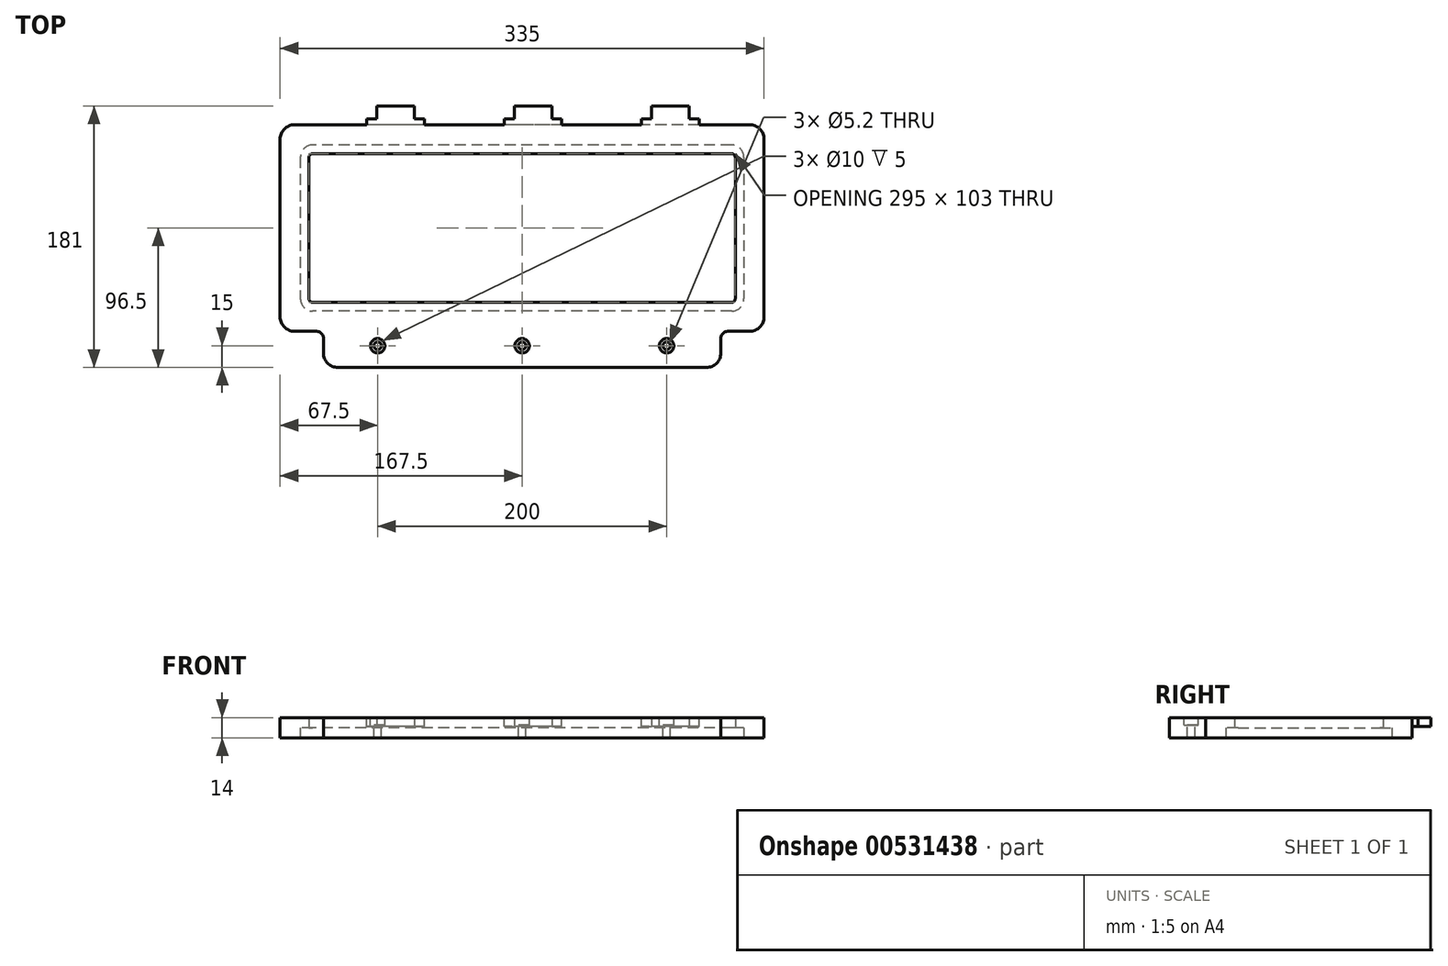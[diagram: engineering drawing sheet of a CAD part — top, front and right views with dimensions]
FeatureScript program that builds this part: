
annotation { "Feature Type Name" : "Feature", "Feature Type Description" : "" }
export const myFeature = defineFeature(function(context is Context, id is Id, definition is map)
    precondition{}
    {
        {
            var Q0;
            Q0=qCreatedBy(makeId("Top.planeOp"),FACE);
            var sketch = newSketch(context, id + "F0", { "sketchPlane" : qUnion([Q0])});
            skLineSegment(sketch, "E0.bottom", {"start": v(145, -51.5) * mm, "end": v(-145, -51.5) * mm});
            skLineSegment(sketch, "E0.top", {"start": v(145, 51.5) * mm, "end": v(-145, 51.5) * mm});
            skLineSegment(sketch, "E0.left", {"start": v(147.5, -49) * mm, "end": v(147.5, 49) * mm});
            skLineSegment(sketch, "E0.right", {"start": v(-147.5, -49) * mm, "end": v(-147.5, 49) * mm});
            skPoint(sketch, "E0.middle", {"position": v(0, 0) * mm});
            skPoint(sketch, "E1.visualSharp", {"position": v(-147.5, 51.5) * mm});
            skArc(sketch, "E1.filletArc", {"start": v(-145, 51.5) * mm, "mid": v(-146.77, 50.77) * mm, "end": v(-147.5, 49) * mm});
            skPoint(sketch, "E2.visualSharp", {"position": v(-147.5, -51.5) * mm});
            skArc(sketch, "E2.filletArc", {"start": v(-147.5, -49) * mm, "mid": v(-146.77, -50.77) * mm, "end": v(-145, -51.5) * mm});
            skPoint(sketch, "E3.visualSharp", {"position": v(147.5, -51.5) * mm});
            skArc(sketch, "E3.filletArc", {"start": v(145, -51.5) * mm, "mid": v(146.77, -50.77) * mm, "end": v(147.5, -49) * mm});
            skPoint(sketch, "E4.visualSharp", {"position": v(147.5, 51.5) * mm});
            skArc(sketch, "E4.filletArc", {"start": v(147.5, 49) * mm, "mid": v(146.77, 50.77) * mm, "end": v(145, 51.5) * mm});
            skLineSegment(sketch, "E5.bottom", {"start": v(167.5, -71.5) * mm, "end": v(137.5, -71.5) * mm});
            skLineSegment(sketch, "E5.top", {"start": v(167.5, 71.5) * mm, "end": v(-167.5, 71.5) * mm});
            skLineSegment(sketch, "E5.left", {"start": v(167.5, -71.5) * mm, "end": v(167.5, 71.5) * mm});
            skLineSegment(sketch, "E5.right", {"start": v(-167.5, -71.5) * mm, "end": v(-167.5, 71.5) * mm});
            skLineSegment(sketch, "E6.top", {"start": v(-137.5, -96.5) * mm, "end": v(137.5, -96.5) * mm});
            skLineSegment(sketch, "E6.left", {"start": v(-137.5, -71.5) * mm, "end": v(-137.5, -96.5) * mm});
            skLineSegment(sketch, "E6.right", {"start": v(137.5, -71.5) * mm, "end": v(137.5, -96.5) * mm});
            skLineSegment(sketch, "E7.trimOffspring", {"start": v(-137.5, -71.5) * mm, "end": v(-167.5, -71.5) * mm});
            skSolve(sketch);
        }
        {
            var Q0;
            Q0=makeQuery(id+"F0.imprint","IMPRINT",FACE,{"disambiguationData":[TD([[makeQuery(id+"F0.imprint","IMPRINT",EDGE,{"derivedFrom":sQuery(id+"F0.wireOp",EDGE,"E0.bottom")}),1.0]])]});
            extrude(context, id + "F1", {"entities" : qUnion([Q0]), "depth" : 14 * mm, "offsetDistance" : 25 * mm});
        }
        {
            var Q0;
            Q0=makeQuery(id+"F1.opExtrude","CAP_FACE",FACE,{"disambiguationData":[OSD([sQuery(id+"F0.wireOp",EDGE,"E0.bottom"),sQuery(id+"F0.wireOp",EDGE,"E0.top"),sQuery(id+"F0.wireOp",EDGE,"E0.left"),sQuery(id+"F0.wireOp",EDGE,"E0.right"),sQuery(id+"F0.wireOp",EDGE,"E1.filletArc"),sQuery(id+"F0.wireOp",EDGE,"E2.filletArc"),sQuery(id+"F0.wireOp",EDGE,"E3.filletArc"),sQuery(id+"F0.wireOp",EDGE,"E4.filletArc"),sQuery(id+"F0.wireOp",EDGE,"E5.bottom"),sQuery(id+"F0.wireOp",EDGE,"E5.top"),sQuery(id+"F0.wireOp",EDGE,"E5.left"),sQuery(id+"F0.wireOp",EDGE,"E5.right")])],"isStart":true});
            var sketch = newSketch(context, id + "F2", { "sketchPlane" : qUnion([Q0])});
            skLineSegment(sketch, "E8.bottom", {"start": v(145, -57.5) * mm, "end": v(-145, -57.5) * mm});
            skLineSegment(sketch, "E8.top", {"start": v(145, 57.5) * mm, "end": v(-145, 57.5) * mm});
            skLineSegment(sketch, "E8.left", {"start": v(153.5, -49) * mm, "end": v(153.5, 49) * mm});
            skLineSegment(sketch, "E8.right", {"start": v(-153.5, -49) * mm, "end": v(-153.5, 49) * mm});
            skPoint(sketch, "E8.middle", {"position": v(0, 0) * mm});
            skPoint(sketch, "E9.visualSharp", {"position": v(-153.5, 57.5) * mm});
            skArc(sketch, "E9.filletArc", {"start": v(-145, 57.5) * mm, "mid": v(-151.01, 55.01) * mm, "end": v(-153.5, 49) * mm});
            skPoint(sketch, "E10.visualSharp", {"position": v(153.5, 57.5) * mm});
            skArc(sketch, "E10.filletArc", {"start": v(153.5, 49) * mm, "mid": v(151.01, 55.01) * mm, "end": v(145, 57.5) * mm});
            skPoint(sketch, "E11.visualSharp", {"position": v(153.5, -57.5) * mm});
            skArc(sketch, "E11.filletArc", {"start": v(145, -57.5) * mm, "mid": v(151.01, -55.01) * mm, "end": v(153.5, -49) * mm});
            skPoint(sketch, "E12.visualSharp", {"position": v(-153.5, -57.5) * mm});
            skArc(sketch, "E12.filletArc", {"start": v(-153.5, -49) * mm, "mid": v(-151.01, -55.01) * mm, "end": v(-145, -57.5) * mm});
            skSolve(sketch);
        }
        {
            var Q0;
            Q0=makeQuery(id+"F2.imprint","IMPRINT",FACE,{"disambiguationData":[TD([[makeQuery(id+"F2.imprint","IMPRINT",EDGE,{"derivedFrom":sQuery(id+"F2.wireOp",EDGE,"E8.bottom")}),-1.0]])]});
            extrude(context, id + "F3", {"entities" : qUnion([Q0]), "operationType" : NewBodyOperationType.REMOVE, "oppositeDirection" : true, "depth" : 7 * mm, "offsetDistance" : 25 * mm});
        }
        {
            var Q0;
            Q0=makeQuery(id+"F1.opExtrude","SWEPT_EDGE",EDGE,{"disambiguationData":[OSD([sQuery(id+"F0.wireOp",EDGE,"E5.right"),sQuery(id+"F0.wireOp",EDGE,"E7.trimOffspring")])]});
            var Q1;
            Q1=makeQuery(id+"F1.opExtrude","SWEPT_EDGE",EDGE,{"disambiguationData":[OSD([sQuery(id+"F0.wireOp",EDGE,"E5.bottom"),sQuery(id+"F0.wireOp",EDGE,"E5.left")])]});
            var Q2;
            Q2=makeQuery(id+"F1.opExtrude","SWEPT_EDGE",EDGE,{"disambiguationData":[OSD([sQuery(id+"F0.wireOp",EDGE,"E6.top"),sQuery(id+"F0.wireOp",EDGE,"E6.right")])]});
            var Q3;
            Q3=makeQuery(id+"F1.opExtrude","SWEPT_EDGE",EDGE,{"disambiguationData":[OSD([sQuery(id+"F0.wireOp",EDGE,"E6.top"),sQuery(id+"F0.wireOp",EDGE,"E6.left")])]});
            var Q4;
            Q4=makeQuery(id+"F1.opExtrude","SWEPT_EDGE",EDGE,{"disambiguationData":[OSD([sQuery(id+"F0.wireOp",EDGE,"E5.top"),sQuery(id+"F0.wireOp",EDGE,"E5.left")])]});
            var Q5;
            Q5=makeQuery(id+"F1.opExtrude","SWEPT_EDGE",EDGE,{"disambiguationData":[OSD([sQuery(id+"F0.wireOp",EDGE,"E5.top"),sQuery(id+"F0.wireOp",EDGE,"E5.right")])]});
            fillet(context, id + "F4", {"entities" : qUnion([Q0, Q1, Q2, Q3, Q4, Q5]), "radius" : 10 * mm, "tangentPropagation" : true, "allowEdgeOverflow" : false});
        }
        {
            var Q0;
            Q0=makeQuery(id+"F1.opExtrude","SWEPT_EDGE",EDGE,{"disambiguationData":[OSD([sQuery(id+"F0.wireOp",EDGE,"E5.bottom"),sQuery(id+"F0.wireOp",EDGE,"E6.right")])]});
            var Q1;
            Q1=makeQuery(id+"F1.opExtrude","SWEPT_EDGE",EDGE,{"disambiguationData":[OSD([sQuery(id+"F0.wireOp",EDGE,"E6.left"),sQuery(id+"F0.wireOp",EDGE,"E7.trimOffspring")])]});
            fillet(context, id + "F5", {"entities" : qUnion([Q0, Q1]), "radius" : 5 * mm, "tangentPropagation" : true, "allowEdgeOverflow" : false});
        }
        {
            var Q0;
            Q0=makeQuery(id+"F1.opExtrude","CAP_FACE",FACE,{"disambiguationData":[OSD([sQuery(id+"F0.wireOp",EDGE,"E0.bottom"),sQuery(id+"F0.wireOp",EDGE,"E0.top"),sQuery(id+"F0.wireOp",EDGE,"E0.left"),sQuery(id+"F0.wireOp",EDGE,"E0.right"),sQuery(id+"F0.wireOp",EDGE,"E1.filletArc"),sQuery(id+"F0.wireOp",EDGE,"E2.filletArc"),sQuery(id+"F0.wireOp",EDGE,"E3.filletArc"),sQuery(id+"F0.wireOp",EDGE,"E4.filletArc"),sQuery(id+"F0.wireOp",EDGE,"E5.bottom"),sQuery(id+"F0.wireOp",EDGE,"E5.top"),sQuery(id+"F0.wireOp",EDGE,"E5.left"),sQuery(id+"F0.wireOp",EDGE,"E5.right"),sQuery(id+"F0.wireOp",EDGE,"E6.top"),sQuery(id+"F0.wireOp",EDGE,"E6.left"),sQuery(id+"F0.wireOp",EDGE,"E6.right"),sQuery(id+"F0.wireOp",EDGE,"E7.trimOffspring")])],"isStart":false});
            var sketch = newSketch(context, id + "F6", { "sketchPlane" : qUnion([Q0])});
            skLineSegment(sketch, "E13", {"start": v(-137.5, -81.5) * mm, "end": v(137.5, -81.5) * mm, "construction": true});
            skCircle(sketch, "E14", {"center": v(0, -81.5) * mm, "radius": 2.6 * mm});
            skCircle(sketch, "E15", {"center": v(-100, -81.5) * mm, "radius": 2.6 * mm});
            skCircle(sketch, "E16", {"center": v(100, -81.5) * mm, "radius": 2.6 * mm});
            skSolve(sketch);
        }
        {
            var Q0;
            Q0=qSketchRegion(id+"F6",true);
            extrude(context, id + "F7", {"entities" : qUnion([Q0]), "operationType" : NewBodyOperationType.REMOVE, "endBound" : BoundingType.THROUGH_ALL, "oppositeDirection" : true, "depth" : 25 * mm, "offsetDistance" : 25 * mm});
        }
        {
            var Q0;
            Q0=makeQuery(id+"F1.opExtrude","CAP_FACE",FACE,{"disambiguationData":[OSD([sQuery(id+"F0.wireOp",EDGE,"E0.bottom"),sQuery(id+"F0.wireOp",EDGE,"E0.top"),sQuery(id+"F0.wireOp",EDGE,"E0.left"),sQuery(id+"F0.wireOp",EDGE,"E0.right"),sQuery(id+"F0.wireOp",EDGE,"E1.filletArc"),sQuery(id+"F0.wireOp",EDGE,"E2.filletArc"),sQuery(id+"F0.wireOp",EDGE,"E3.filletArc"),sQuery(id+"F0.wireOp",EDGE,"E4.filletArc"),sQuery(id+"F0.wireOp",EDGE,"E5.bottom"),sQuery(id+"F0.wireOp",EDGE,"E5.top"),sQuery(id+"F0.wireOp",EDGE,"E5.left"),sQuery(id+"F0.wireOp",EDGE,"E5.right"),sQuery(id+"F0.wireOp",EDGE,"E6.top"),sQuery(id+"F0.wireOp",EDGE,"E6.left"),sQuery(id+"F0.wireOp",EDGE,"E6.right"),sQuery(id+"F0.wireOp",EDGE,"E7.trimOffspring")])],"isStart":false});
            var sketch = newSketch(context, id + "F8", { "sketchPlane" : qUnion([Q0])});
            skCircle(sketch, "E17", {"center": v(-100, -81.5) * mm, "radius": 5 * mm});
            skCircle(sketch, "E18", {"center": v(0, -81.5) * mm, "radius": 5 * mm});
            skCircle(sketch, "E19", {"center": v(100, -81.5) * mm, "radius": 5 * mm});
            skSolve(sketch);
        }
        {
            var Q0;
            Q0=qSketchRegion(id+"F8",true);
            extrude(context, id + "F9", {"entities" : qUnion([Q0]), "operationType" : NewBodyOperationType.REMOVE, "oppositeDirection" : true, "depth" : 5 * mm, "offsetDistance" : 25 * mm});
        }
        {
            var Q0;
            Q0=makeQuery(id+"F1.opExtrude","SWEPT_FACE",FACE,{"disambiguationData":[OSD([sQuery(id+"F0.wireOp",EDGE,"E5.top")])]});
            var sketch = newSketch(context, id + "F10", { "sketchPlane" : qUnion([Q0])});
            skLineSegment(sketch, "E20", {"start": v(-177.46, 8) * mm, "end": v(173.74, 8) * mm, "construction": true});
            skLineSegment(sketch, "E21.bottom", {"start": v(-115.5, 8) * mm, "end": v(-89.5, 8) * mm});
            skLineSegment(sketch, "E21.top", {"start": v(-115.5, 14) * mm, "end": v(-89.5, 14) * mm});
            skLineSegment(sketch, "E21.left", {"start": v(-115.5, 8) * mm, "end": v(-115.5, 14) * mm});
            skLineSegment(sketch, "E21.right", {"start": v(-89.5, 8) * mm, "end": v(-89.5, 14) * mm});
            skLineSegment(sketch, "E22.bottom", {"start": v(-20.5, 8) * mm, "end": v(5.5, 8) * mm});
            skLineSegment(sketch, "E22.top", {"start": v(-20.5, 14) * mm, "end": v(5.5, 14) * mm});
            skLineSegment(sketch, "E22.left", {"start": v(-20.5, 8) * mm, "end": v(-20.5, 14) * mm});
            skLineSegment(sketch, "E22.right", {"start": v(5.5, 8) * mm, "end": v(5.5, 14) * mm});
            skLineSegment(sketch, "E23.bottom", {"start": v(74.5, 8) * mm, "end": v(100.5, 8) * mm});
            skLineSegment(sketch, "E23.top", {"start": v(74.5, 14) * mm, "end": v(100.5, 14) * mm});
            skLineSegment(sketch, "E23.left", {"start": v(74.5, 8) * mm, "end": v(74.5, 14) * mm});
            skLineSegment(sketch, "E23.right", {"start": v(100.5, 8) * mm, "end": v(100.5, 14) * mm});
            skSolve(sketch);
        }
        {
            var Q0;
            Q0=qSketchRegion(id+"F10",true);
            extrude(context, id + "F11", {"entities" : qUnion([Q0]), "operationType" : NewBodyOperationType.ADD, "depth" : 13 * mm, "offsetDistance" : 25 * mm});
        }
        {
            var Q0;
            Q0=makeQuery(id+"F11.boolean.opBoolean","MERGE",FACE,{"derivedFrom":[makeQuery(id+"F1.opExtrude","CAP_FACE",FACE,{"disambiguationData":[OSD([sQuery(id+"F0.wireOp",EDGE,"E0.bottom"),sQuery(id+"F0.wireOp",EDGE,"E0.top"),sQuery(id+"F0.wireOp",EDGE,"E0.left"),sQuery(id+"F0.wireOp",EDGE,"E0.right"),sQuery(id+"F0.wireOp",EDGE,"E1.filletArc"),sQuery(id+"F0.wireOp",EDGE,"E2.filletArc"),sQuery(id+"F0.wireOp",EDGE,"E3.filletArc"),sQuery(id+"F0.wireOp",EDGE,"E4.filletArc"),sQuery(id+"F0.wireOp",EDGE,"E5.bottom"),sQuery(id+"F0.wireOp",EDGE,"E5.top"),sQuery(id+"F0.wireOp",EDGE,"E5.left"),sQuery(id+"F0.wireOp",EDGE,"E5.right"),sQuery(id+"F0.wireOp",EDGE,"E6.top"),sQuery(id+"F0.wireOp",EDGE,"E6.left"),sQuery(id+"F0.wireOp",EDGE,"E6.right"),sQuery(id+"F0.wireOp",EDGE,"E7.trimOffspring")])],"isStart":false}),makeQuery(id+"F11.opExtrude","SWEPT_FACE",FACE,{"disambiguationData":[OSD([sQuery(id+"F10.wireOp",EDGE,"E21.top")])]}),makeQuery(id+"F11.opExtrude","SWEPT_FACE",FACE,{"disambiguationData":[OSD([sQuery(id+"F10.wireOp",EDGE,"E22.top")])]}),makeQuery(id+"F11.opExtrude","SWEPT_FACE",FACE,{"disambiguationData":[OSD([sQuery(id+"F10.wireOp",EDGE,"E23.top")])]})]});
            var sketch = newSketch(context, id + "F12", { "sketchPlane" : qUnion([Q0])});
            skLineSegment(sketch, "E24.bottom", {"start": v(-107.5, 75.5) * mm, "end": v(-67.5, 75.5) * mm});
            skLineSegment(sketch, "E24.top", {"start": v(-107.5, 71.5) * mm, "end": v(-67.5, 71.5) * mm});
            skLineSegment(sketch, "E24.left", {"start": v(-107.5, 75.5) * mm, "end": v(-107.5, 71.5) * mm});
            skLineSegment(sketch, "E24.right", {"start": v(-67.5, 75.5) * mm, "end": v(-67.5, 71.5) * mm});
            skLineSegment(sketch, "E25.bottom", {"start": v(-12.5, 75.5) * mm, "end": v(27.5, 75.5) * mm});
            skLineSegment(sketch, "E25.top", {"start": v(-12.5, 71.5) * mm, "end": v(27.5, 71.5) * mm});
            skLineSegment(sketch, "E25.left", {"start": v(-12.5, 75.5) * mm, "end": v(-12.5, 71.5) * mm});
            skLineSegment(sketch, "E25.right", {"start": v(27.5, 75.5) * mm, "end": v(27.5, 71.5) * mm});
            skLineSegment(sketch, "E26.bottom", {"start": v(82.5, 71.5) * mm, "end": v(122.5, 71.5) * mm});
            skLineSegment(sketch, "E26.top", {"start": v(82.5, 75.5) * mm, "end": v(122.5, 75.5) * mm});
            skLineSegment(sketch, "E26.left", {"start": v(82.5, 71.5) * mm, "end": v(82.5, 75.5) * mm});
            skLineSegment(sketch, "E26.right", {"start": v(122.5, 71.5) * mm, "end": v(122.5, 75.5) * mm});
            skSolve(sketch);
        }
        {
            var Q0;
            Q0=qSketchRegion(id+"F12",true);
            extrude(context, id + "F13", {"entities" : qUnion([Q0]), "operationType" : NewBodyOperationType.ADD, "oppositeDirection" : true, "depth" : 6 * mm, "offsetDistance" : 25 * mm});
        }
    });
